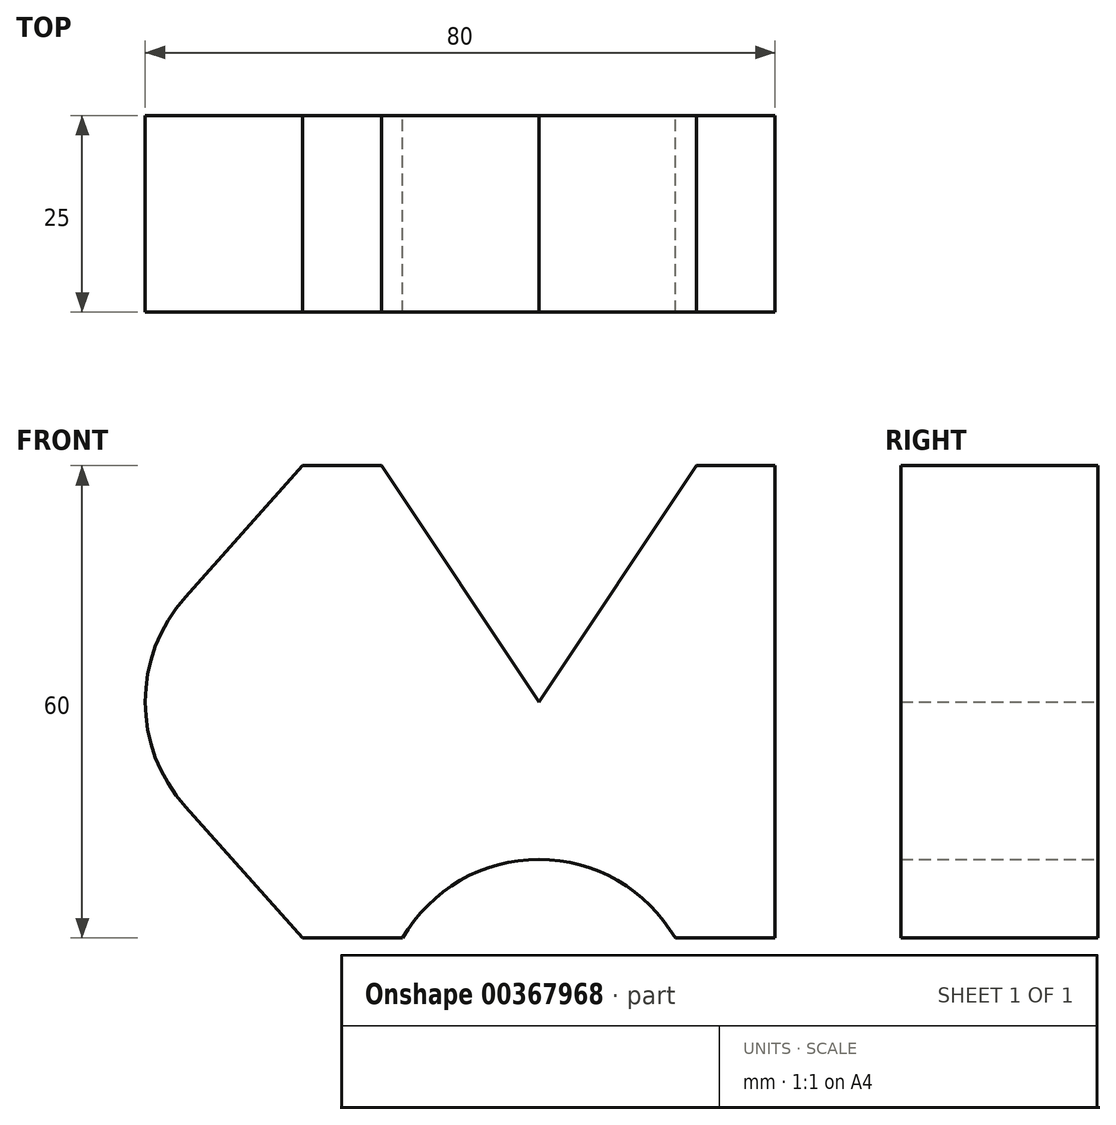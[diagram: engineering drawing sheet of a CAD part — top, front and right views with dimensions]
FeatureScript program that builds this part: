
annotation { "Feature Type Name" : "Feature", "Feature Type Description" : "" }
export const myFeature = defineFeature(function(context is Context, id is Id, definition is map)
    precondition{}
    {
        {
            var Q0;
            Q0=qCreatedBy(makeId("Front.planeOp"),FACE);
            var sketch = newSketch(context, id + "F0", { "sketchPlane" : qUnion([Q0])});
            skLineSegment(sketch, "E0", {"start": v(0, 0) * mm, "end": v(20, 30) * mm});
            skLineSegment(sketch, "E1", {"start": v(20, 30) * mm, "end": v(30, 30) * mm});
            skLineSegment(sketch, "E2", {"start": v(30, 30) * mm, "end": v(30, -30) * mm});
            skLineSegment(sketch, "E3", {"start": v(30, -30) * mm, "end": v(17.32, -30) * mm});
            skArc(sketch, "E4", {"start": v(17.32, -30) * mm, "mid": v(0, -20) * mm, "end": v(-17.32, -30) * mm});
            skLineSegment(sketch, "E5", {"start": v(-17.32, -30) * mm, "end": v(-30, -30) * mm});
            skLineSegment(sketch, "E6", {"start": v(-30, -30) * mm, "end": v(-44.9, -13.33) * mm});
            skArc(sketch, "E7", {"start": v(-44.9, 13.33) * mm, "mid": v(-50, 0) * mm, "end": v(-44.9, -13.33) * mm});
            skLineSegment(sketch, "E8", {"start": v(-44.9, 13.33) * mm, "end": v(-30, 30) * mm});
            skLineSegment(sketch, "E9", {"start": v(-30, 30) * mm, "end": v(-20, 30) * mm});
            skLineSegment(sketch, "E10", {"start": v(-20, 30) * mm, "end": v(0, 0) * mm});
            skLineSegment(sketch, "E11", {"start": v(-30, 30) * mm, "end": v(-30, -30) * mm, "construction": true});
            skSolve(sketch);
        }
        {
            var Q0;
            Q0 = qSketchRegion(id + "F0", true);
            extrude(context, id + "F1", {"entities" : qUnion([Q0]), "depth" : 25 * mm});
        }
    });
